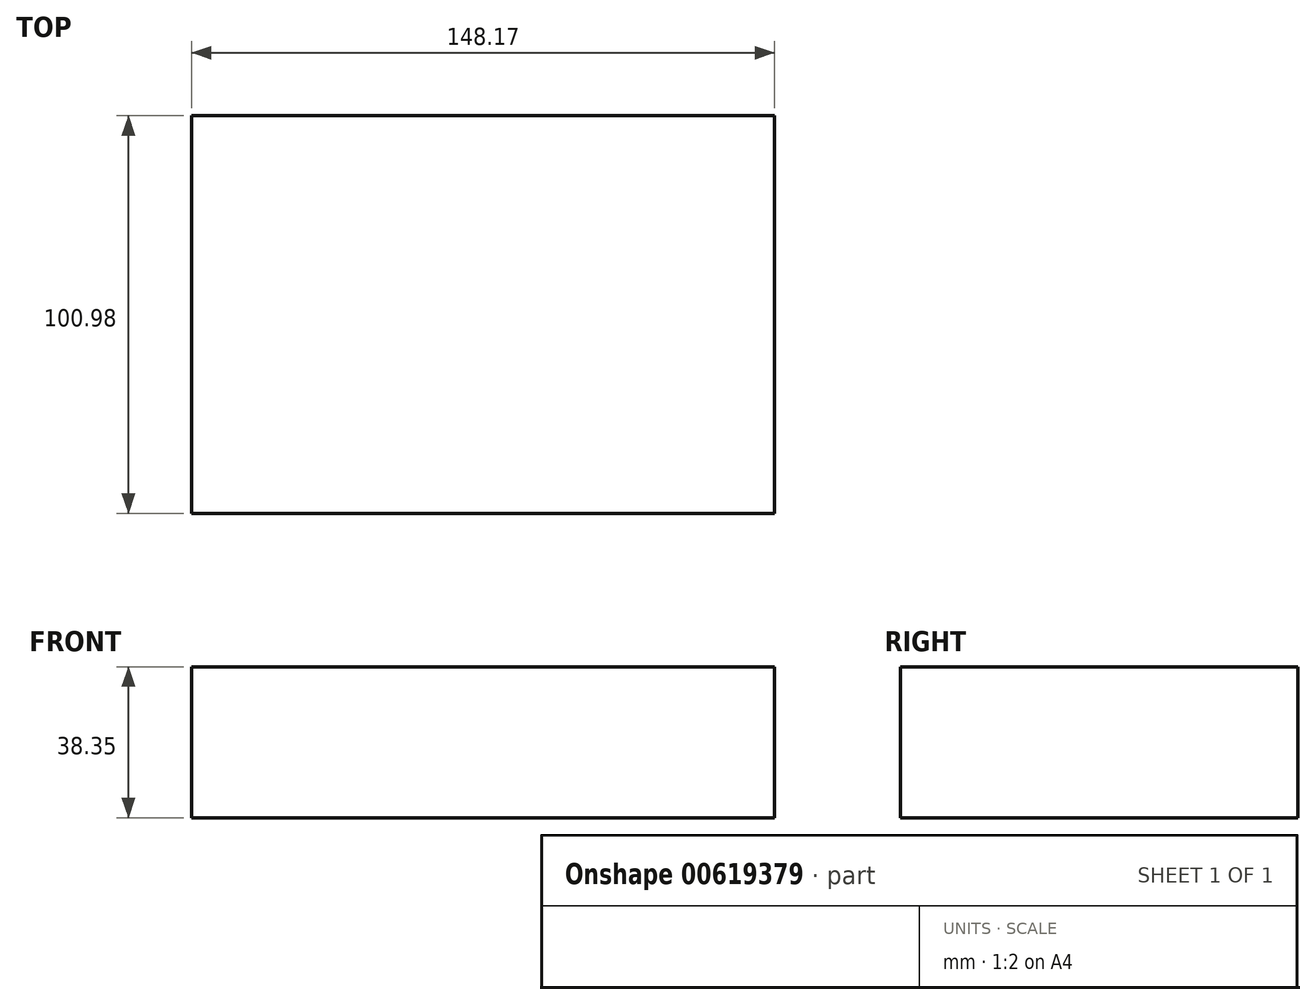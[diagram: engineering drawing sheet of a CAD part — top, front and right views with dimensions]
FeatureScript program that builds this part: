
annotation { "Feature Type Name" : "Feature", "Feature Type Description" : "" }
export const myFeature = defineFeature(function(context is Context, id is Id, definition is map)
    precondition{}
    {
        {
            var Q0;
            Q0=qCreatedBy(makeId("Top.planeOp"),FACE);
            var sketch = newSketch(context, id + "F0", { "sketchPlane" : qUnion([Q0])});
            skLineSegment(sketch, "E0.bottom", {"start": v(-96.4, 45.07) * mm, "end": v(51.78, 45.07) * mm});
            skLineSegment(sketch, "E0.top", {"start": v(-96.4, -55.9) * mm, "end": v(51.78, -55.9) * mm});
            skLineSegment(sketch, "E0.left", {"start": v(-96.4, 45.07) * mm, "end": v(-96.4, -55.9) * mm});
            skLineSegment(sketch, "E0.right", {"start": v(51.78, 45.07) * mm, "end": v(51.78, -55.9) * mm});
            skSolve(sketch);
        }
        {
            var Q0;
            Q0=makeQuery(id+"F0.imprint","IMPRINT",FACE,{"disambiguationData":[TD([[makeQuery(id+"F0.imprint","IMPRINT",EDGE,{"derivedFrom":sQuery(id+"F0.wireOp",EDGE,"E0.bottom")}),-1.0]])]});
            extrude(context, id + "F1", {"entities" : qUnion([Q0]), "depth" : 38.35 * mm, "offsetDistance" : 25.4 * mm});
        }
    });
